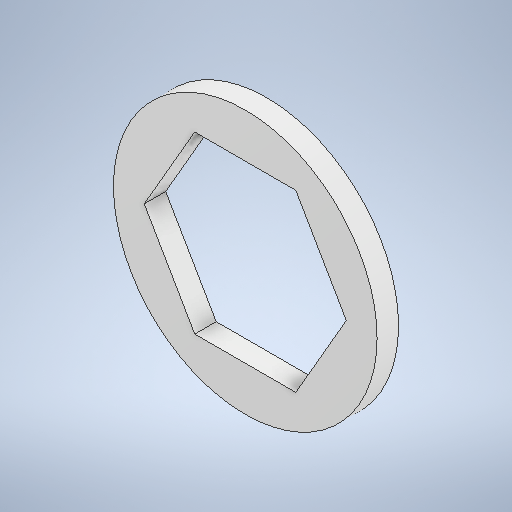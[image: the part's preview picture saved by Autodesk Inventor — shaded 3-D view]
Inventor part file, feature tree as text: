
AUTODESK INVENTOR PART (.ipt)
format: ipt  version: 2025.1 (Build 291241020, 241B)  size: 247,808 bytes
history: native  units: in
note: dims shown in document units (in); Inventor stores cm internally (conversion verified against a paired STEP export)
features: extrude x1, sketch x1
ambient origin geometry x8: Origin, YZ Plane, XZ Plane, XY Plane, X Axis, Y Axis, Z Axis, Center Point
bodies: Solid1 (feature_tree)
feature tree (2):
  extrude  "Extrusion1"  Depth=0.51in
  sketch  "Sketch1"  dims[d0=0.768in d1=0.51in d2=0.0625in d3=0.0in]
